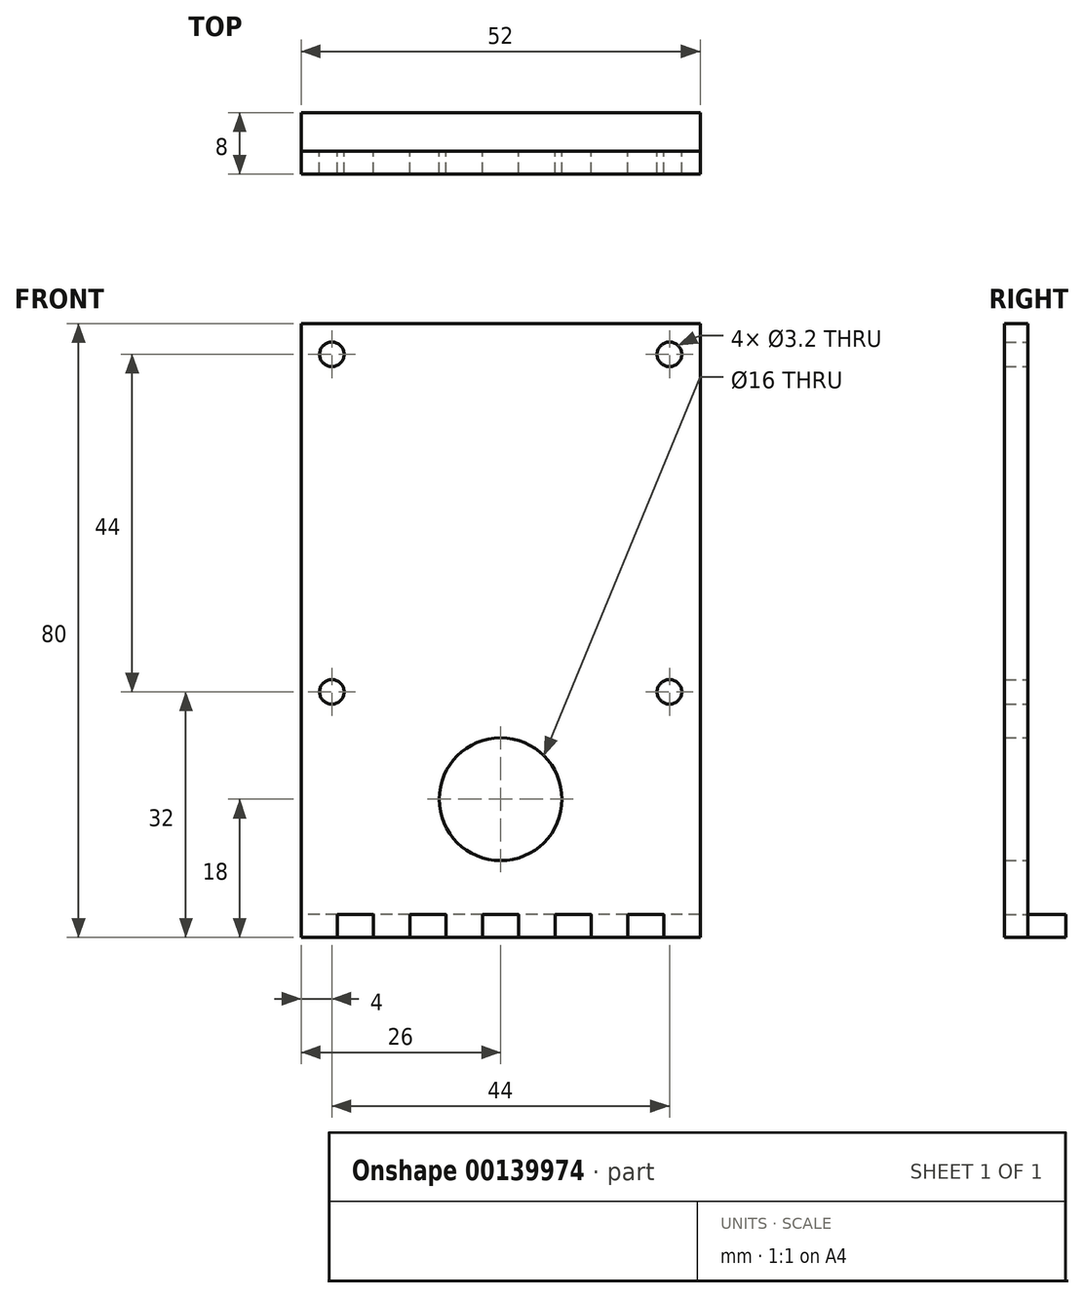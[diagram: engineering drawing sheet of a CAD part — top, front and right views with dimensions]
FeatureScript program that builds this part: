
annotation { "Feature Type Name" : "Feature", "Feature Type Description" : "" }
export const myFeature = defineFeature(function(context is Context, id is Id, definition is map)
    precondition{}
    {
        {
            var Q0;
            Q0=qCreatedBy(makeId("Front.planeOp"),FACE);
            var sketch = newSketch(context, id + "F0", { "sketchPlane" : qUnion([Q0])});
            skLineSegment(sketch, "E0.bottom", {"start": v(0, 0) * mm, "end": v(4.73, 0) * mm});
            skLineSegment(sketch, "E0.top", {"start": v(0, 80) * mm, "end": v(52, 80) * mm});
            skLineSegment(sketch, "E0.left", {"start": v(0, 0) * mm, "end": v(0, 80) * mm});
            skLineSegment(sketch, "E0.right", {"start": v(52, 0) * mm, "end": v(52, 80) * mm});
            skLineSegment(sketch, "E1", {"start": v(28.36, 3) * mm, "end": v(28.36, 0) * mm});
            skLineSegment(sketch, "E2", {"start": v(33.1, 0) * mm, "end": v(33.1, 3) * mm});
            skLineSegment(sketch, "E3", {"start": v(33.1, 3) * mm, "end": v(37.82, 3) * mm});
            skLineSegment(sketch, "E4", {"start": v(37.82, 3) * mm, "end": v(37.82, 0) * mm});
            skLineSegment(sketch, "E5", {"start": v(42.55, 0) * mm, "end": v(42.55, 3) * mm});
            skLineSegment(sketch, "E6", {"start": v(42.55, 3) * mm, "end": v(47.27, 3) * mm});
            skLineSegment(sketch, "E7", {"start": v(47.27, 3) * mm, "end": v(47.27, 0) * mm});
            skLineSegment(sketch, "E8.trimOffspring", {"start": v(28.36, 0) * mm, "end": v(33.1, 0) * mm});
            skLineSegment(sketch, "E9.trimOffspring", {"start": v(37.82, 0) * mm, "end": v(42.55, 0) * mm});
            skLineSegment(sketch, "E10.trimOffspring", {"start": v(47.27, 0) * mm, "end": v(52, 0) * mm});
            skLineSegment(sketch, "E11", {"start": v(4.73, 0) * mm, "end": v(4.73, 3) * mm});
            skLineSegment(sketch, "E12", {"start": v(4.73, 3) * mm, "end": v(9.45, 3) * mm});
            skLineSegment(sketch, "E13", {"start": v(9.45, 3) * mm, "end": v(9.45, 0) * mm});
            skLineSegment(sketch, "E14", {"start": v(9.45, 0) * mm, "end": v(14.18, 0) * mm});
            skLineSegment(sketch, "E15", {"start": v(14.18, 0) * mm, "end": v(14.18, 3) * mm});
            skLineSegment(sketch, "E16", {"start": v(14.18, 3) * mm, "end": v(18.9, 3) * mm});
            skLineSegment(sketch, "E17", {"start": v(18.9, 3) * mm, "end": v(18.9, 0) * mm});
            skLineSegment(sketch, "E18", {"start": v(18.9, 0) * mm, "end": v(23.64, 0) * mm});
            skLineSegment(sketch, "E19", {"start": v(23.64, 0) * mm, "end": v(23.64, 3) * mm});
            skLineSegment(sketch, "E20", {"start": v(23.64, 3) * mm, "end": v(28.36, 3) * mm});
            skLineSegment(sketch, "E21.bottom", {"start": v(4, 76) * mm, "end": v(48, 76) * mm, "construction": true});
            skLineSegment(sketch, "E21.top", {"start": v(4, 32) * mm, "end": v(48, 32) * mm, "construction": true});
            skLineSegment(sketch, "E21.left", {"start": v(4, 76) * mm, "end": v(4, 32) * mm, "construction": true});
            skLineSegment(sketch, "E21.right", {"start": v(48, 76) * mm, "end": v(48, 32) * mm, "construction": true});
            skLineSegment(sketch, "E22", {"start": v(0, 76) * mm, "end": v(4, 76) * mm, "construction": true});
            skLineSegment(sketch, "E23", {"start": v(4, 76) * mm, "end": v(4, 80) * mm, "construction": true});
            skLineSegment(sketch, "E24", {"start": v(48, 76) * mm, "end": v(52, 76) * mm, "construction": true});
            skCircle(sketch, "E25", {"center": v(4, 76) * mm, "radius": 1.6 * mm});
            skCircle(sketch, "E26", {"center": v(48, 76) * mm, "radius": 1.6 * mm});
            skCircle(sketch, "E27", {"center": v(4, 32) * mm, "radius": 1.6 * mm});
            skCircle(sketch, "E28", {"center": v(48, 32) * mm, "radius": 1.6 * mm});
            skCircle(sketch, "E29", {"center": v(26, 18) * mm, "radius": 8 * mm});
            skLineSegment(sketch, "E30", {"start": v(26, 80) * mm, "end": v(26, 32) * mm, "construction": true});
            skSolve(sketch);
        }
        {
            var Q0;
            Q0=makeQuery(id+"F0.imprint","IMPRINT",FACE,{"disambiguationData":[TD([[makeQuery(id+"F0.imprint","IMPRINT",EDGE,{"derivedFrom":sQuery(id+"F0.wireOp",EDGE,"E0.bottom")}),1.0]])]});
            var Q1;
            {var subQ6=sQuery(id+"F0.wireOp",EDGE,"E4");Q1=makeQuery(id+"F0.imprint","IMPRINT",FACE,{"disambiguationData":[TD([[makeQuery(id+"F0.imprint","IMPRINT",EDGE,{"derivedFrom":subQ6}),1.0]])]});}
            extrude(context, id + "F1", {"entities" : qUnion([Q0, Q1]), "depth" : 3 * mm});
        }
        {
            var Q0;
            Q0=makeQuery(id+"F1.opExtrude","CAP_FACE",FACE,{"disambiguationData":[OSD([sQuery(id+"F0.wireOp",EDGE,"E0.bottom"),sQuery(id+"F0.wireOp",EDGE,"E0.top"),sQuery(id+"F0.wireOp",EDGE,"E0.left"),sQuery(id+"F0.wireOp",EDGE,"E0.right"),sQuery(id+"F0.wireOp",EDGE,"E1"),sQuery(id+"F0.wireOp",EDGE,"E2"),sQuery(id+"F0.wireOp",EDGE,"E3"),sQuery(id+"F0.wireOp",EDGE,"E4"),sQuery(id+"F0.wireOp",EDGE,"E5"),sQuery(id+"F0.wireOp",EDGE,"E6"),sQuery(id+"F0.wireOp",EDGE,"PKkihstR-OvO3-Emr3-Gdbt-astjGcmU0KQB"),sQuery(id+"F0.wireOp",EDGE,"1ep62Iue-U5LH-vBv7-MXpD-Muabvh4OJFxf"),sQuery(id+"F0.wireOp",EDGE,"l2Q62QRf-urln-dHTa-iypO-8Orn8cwlWFba"),sQuery(id+"F0.wireOp",EDGE,"E7"),sQuery(id+"F0.wireOp",EDGE,"b9FiUV6K-tjbD-lqSt-eLXH-odPebWflUP3h"),sQuery(id+"F0.wireOp",EDGE,"AiMVLUEX-WyG6-zVHs-gMEj-qvYr0DqTvYnE"),sQuery(id+"F0.wireOp",EDGE,"VuksS3ty-KPdi-KyUG-c4xT-hWloxtrvA3Kk"),sQuery(id+"F0.wireOp",EDGE,"E8.trimOffspring"),sQuery(id+"F0.wireOp",EDGE,"E9.trimOffspring"),sQuery(id+"F0.wireOp",EDGE,"dc53b560-5744-44dd-9cf0-b4f1f6c820a9.trimOffspring"),sQuery(id+"F0.wireOp",EDGE,"b14e94e7-d7bf-4d2a-936f-5f05cbea75e0.trimOffspring"),sQuery(id+"F0.wireOp",EDGE,"E10.trimOffspring"),sQuery(id+"F0.wireOp",EDGE,"E11"),sQuery(id+"F0.wireOp",EDGE,"E12"),sQuery(id+"F0.wireOp",EDGE,"E13"),sQuery(id+"F0.wireOp",EDGE,"E14"),sQuery(id+"F0.wireOp",EDGE,"E15"),sQuery(id+"F0.wireOp",EDGE,"E16"),sQuery(id+"F0.wireOp",EDGE,"E17"),sQuery(id+"F0.wireOp",EDGE,"E18"),sQuery(id+"F0.wireOp",EDGE,"E19"),sQuery(id+"F0.wireOp",EDGE,"E20")])],"isStart":false});
            var sketch = newSketch(context, id + "F2", { "sketchPlane" : qUnion([Q0])});
            skLineSegment(sketch, "E31.bottom", {"start": v(0, 0) * mm, "end": v(52, 0) * mm});
            skLineSegment(sketch, "E31.top", {"start": v(0, 3) * mm, "end": v(52, 3) * mm});
            skLineSegment(sketch, "E31.left", {"start": v(0, 0) * mm, "end": v(0, 3) * mm});
            skLineSegment(sketch, "E31.right", {"start": v(52, 0) * mm, "end": v(52, 3) * mm});
            skSolve(sketch);
        }
        {
            var Q0;
            {var subQ0=sQuery(id+"F2.wireOp",EDGE,"E31.left");Q0=makeQuery(id+"F2.imprint","IMPRINT",FACE,{"disambiguationData":[TD([[makeQuery(id+"F2.imprint","IMPRINT",EDGE,{"derivedFrom":subQ0}),-1.0]])]});}
            var Q1;
            {var subQ1=makeQuery(id+"F1.opExtrude","CAP_EDGE",EDGE,{"disambiguationData":[OSD([sQuery(id+"F0.wireOp",EDGE,"E11")])],"isStart":false});Q1=makeQuery(id+"F2.imprint","IMPRINT",FACE,{"disambiguationData":[TD([[makeQuery(id+"F2.imprint","IMPRINT",EDGE,{"derivedFrom":subQ1}),-1.0]])]});}
            var Q2;
            {var subQ1=makeQuery(id+"F1.opExtrude","CAP_EDGE",EDGE,{"disambiguationData":[OSD([sQuery(id+"F0.wireOp",EDGE,"E13")])],"isStart":false});Q2=makeQuery(id+"F2.imprint","IMPRINT",FACE,{"disambiguationData":[TD([[makeQuery(id+"F2.imprint","IMPRINT",EDGE,{"derivedFrom":subQ1}),1.0]])]});}
            var Q3;
            {var subQ1=makeQuery(id+"F1.opExtrude","CAP_EDGE",EDGE,{"disambiguationData":[OSD([sQuery(id+"F0.wireOp",EDGE,"E15")])],"isStart":false});Q3=makeQuery(id+"F2.imprint","IMPRINT",FACE,{"disambiguationData":[TD([[makeQuery(id+"F2.imprint","IMPRINT",EDGE,{"derivedFrom":subQ1}),-1.0]])]});}
            var Q4;
            {var subQ1=makeQuery(id+"F1.opExtrude","CAP_EDGE",EDGE,{"disambiguationData":[OSD([sQuery(id+"F0.wireOp",EDGE,"E17")])],"isStart":false});Q4=makeQuery(id+"F2.imprint","IMPRINT",FACE,{"disambiguationData":[TD([[makeQuery(id+"F2.imprint","IMPRINT",EDGE,{"derivedFrom":subQ1}),1.0]])]});}
            var Q5;
            {var subQ1=makeQuery(id+"F1.opExtrude","CAP_EDGE",EDGE,{"disambiguationData":[OSD([sQuery(id+"F0.wireOp",EDGE,"E1")])],"isStart":false});Q5=makeQuery(id+"F2.imprint","IMPRINT",FACE,{"disambiguationData":[TD([[makeQuery(id+"F2.imprint","IMPRINT",EDGE,{"derivedFrom":subQ1}),-1.0]])]});}
            var Q6;
            {var subQ1=makeQuery(id+"F1.opExtrude","CAP_EDGE",EDGE,{"disambiguationData":[OSD([sQuery(id+"F0.wireOp",EDGE,"E1")])],"isStart":false});Q6=makeQuery(id+"F2.imprint","IMPRINT",FACE,{"disambiguationData":[TD([[makeQuery(id+"F2.imprint","IMPRINT",EDGE,{"derivedFrom":subQ1}),1.0]])]});}
            var Q7;
            {var subQ1=makeQuery(id+"F1.opExtrude","CAP_EDGE",EDGE,{"disambiguationData":[OSD([sQuery(id+"F0.wireOp",EDGE,"E2")])],"isStart":false});Q7=makeQuery(id+"F2.imprint","IMPRINT",FACE,{"disambiguationData":[TD([[makeQuery(id+"F2.imprint","IMPRINT",EDGE,{"derivedFrom":subQ1}),-1.0]])]});}
            var Q8;
            {var subQ1=makeQuery(id+"F1.opExtrude","CAP_EDGE",EDGE,{"disambiguationData":[OSD([sQuery(id+"F0.wireOp",EDGE,"E4")])],"isStart":false});Q8=makeQuery(id+"F2.imprint","IMPRINT",FACE,{"disambiguationData":[TD([[makeQuery(id+"F2.imprint","IMPRINT",EDGE,{"derivedFrom":subQ1}),1.0]])]});}
            var Q9;
            {var subQ1=makeQuery(id+"F1.opExtrude","CAP_EDGE",EDGE,{"disambiguationData":[OSD([sQuery(id+"F0.wireOp",EDGE,"E5")])],"isStart":false});Q9=makeQuery(id+"F2.imprint","IMPRINT",FACE,{"disambiguationData":[TD([[makeQuery(id+"F2.imprint","IMPRINT",EDGE,{"derivedFrom":subQ1}),-1.0]])]});}
            var Q10;
            {var subQ1=makeQuery(id+"F1.opExtrude","CAP_EDGE",EDGE,{"disambiguationData":[OSD([sQuery(id+"F0.wireOp",EDGE,"PKkihstR-OvO3-Emr3-Gdbt-astjGcmU0KQB")])],"isStart":false});Q10=makeQuery(id+"F2.imprint","IMPRINT",FACE,{"disambiguationData":[TD([[makeQuery(id+"F2.imprint","IMPRINT",EDGE,{"derivedFrom":subQ1}),1.0]])]});}
            var Q11;
            {var subQ1=makeQuery(id+"F1.opExtrude","CAP_EDGE",EDGE,{"disambiguationData":[OSD([sQuery(id+"F0.wireOp",EDGE,"1ep62Iue-U5LH-vBv7-MXpD-Muabvh4OJFxf")])],"isStart":false});Q11=makeQuery(id+"F2.imprint","IMPRINT",FACE,{"disambiguationData":[TD([[makeQuery(id+"F2.imprint","IMPRINT",EDGE,{"derivedFrom":subQ1}),-1.0]])]});}
            var Q12;
            {var subQ1=makeQuery(id+"F1.opExtrude","CAP_EDGE",EDGE,{"disambiguationData":[OSD([sQuery(id+"F0.wireOp",EDGE,"E7")])],"isStart":false});Q12=makeQuery(id+"F2.imprint","IMPRINT",FACE,{"disambiguationData":[TD([[makeQuery(id+"F2.imprint","IMPRINT",EDGE,{"derivedFrom":subQ1}),1.0]])]});}
            var Q13;
            {var subQ1=makeQuery(id+"F1.opExtrude","CAP_EDGE",EDGE,{"disambiguationData":[OSD([sQuery(id+"F0.wireOp",EDGE,"b9FiUV6K-tjbD-lqSt-eLXH-odPebWflUP3h")])],"isStart":false});Q13=makeQuery(id+"F2.imprint","IMPRINT",FACE,{"disambiguationData":[TD([[makeQuery(id+"F2.imprint","IMPRINT",EDGE,{"derivedFrom":subQ1}),-1.0]])]});}
            var Q14;
            {var subQ0=sQuery(id+"F2.wireOp",EDGE,"E31.right");Q14=makeQuery(id+"F2.imprint","IMPRINT",FACE,{"disambiguationData":[TD([[makeQuery(id+"F2.imprint","IMPRINT",EDGE,{"derivedFrom":subQ0}),1.0]])]});}
            extrude(context, id + "F3", {"entities" : qUnion([Q0, Q1, Q2, Q3, Q4, Q5, Q6, Q7, Q8, Q9, Q10, Q11, Q12, Q13, Q14]), "oppositeDirection" : true, "depth" : 8 * mm});
        }
        {
            var Q0;
            Q0=makeQuery(id+"F1.opExtrude","SWEPT_BODY",BODY,{"disambiguationData":[OSD([sQuery(id+"F0.wireOp",EDGE,"E0.bottom"),sQuery(id+"F0.wireOp",EDGE,"E0.top"),sQuery(id+"F0.wireOp",EDGE,"E0.left"),sQuery(id+"F0.wireOp",EDGE,"E0.right"),sQuery(id+"F0.wireOp",EDGE,"E1"),sQuery(id+"F0.wireOp",EDGE,"E2"),sQuery(id+"F0.wireOp",EDGE,"E3"),sQuery(id+"F0.wireOp",EDGE,"E4"),sQuery(id+"F0.wireOp",EDGE,"E5"),sQuery(id+"F0.wireOp",EDGE,"E6"),sQuery(id+"F0.wireOp",EDGE,"PKkihstR-OvO3-Emr3-Gdbt-astjGcmU0KQB"),sQuery(id+"F0.wireOp",EDGE,"1ep62Iue-U5LH-vBv7-MXpD-Muabvh4OJFxf"),sQuery(id+"F0.wireOp",EDGE,"l2Q62QRf-urln-dHTa-iypO-8Orn8cwlWFba"),sQuery(id+"F0.wireOp",EDGE,"E7"),sQuery(id+"F0.wireOp",EDGE,"b9FiUV6K-tjbD-lqSt-eLXH-odPebWflUP3h"),sQuery(id+"F0.wireOp",EDGE,"AiMVLUEX-WyG6-zVHs-gMEj-qvYr0DqTvYnE"),sQuery(id+"F0.wireOp",EDGE,"VuksS3ty-KPdi-KyUG-c4xT-hWloxtrvA3Kk"),sQuery(id+"F0.wireOp",EDGE,"E8.trimOffspring"),sQuery(id+"F0.wireOp",EDGE,"E9.trimOffspring"),sQuery(id+"F0.wireOp",EDGE,"dc53b560-5744-44dd-9cf0-b4f1f6c820a9.trimOffspring"),sQuery(id+"F0.wireOp",EDGE,"b14e94e7-d7bf-4d2a-936f-5f05cbea75e0.trimOffspring"),sQuery(id+"F0.wireOp",EDGE,"E10.trimOffspring"),sQuery(id+"F0.wireOp",EDGE,"E11"),sQuery(id+"F0.wireOp",EDGE,"E12"),sQuery(id+"F0.wireOp",EDGE,"E13"),sQuery(id+"F0.wireOp",EDGE,"E14"),sQuery(id+"F0.wireOp",EDGE,"E15"),sQuery(id+"F0.wireOp",EDGE,"E16"),sQuery(id+"F0.wireOp",EDGE,"E17"),sQuery(id+"F0.wireOp",EDGE,"E18"),sQuery(id+"F0.wireOp",EDGE,"E19"),sQuery(id+"F0.wireOp",EDGE,"E20")])]});
            var Q1;
            Q1=makeQuery(id+"F3.opExtrude","SWEPT_BODY",BODY,{"disambiguationData":[OSD([sQuery(id+"F2.wireOp",EDGE,"E31.bottom"),sQuery(id+"F2.wireOp",EDGE,"E31.top"),sQuery(id+"F2.wireOp",EDGE,"E31.left"),sQuery(id+"F2.wireOp",EDGE,"E31.right")])]});
            booleanBodies(context, id + "F4", {"operationType" : BooleanOperationType.SUBTRACTION, "tools" : qUnion([Q0]), "targets" : qUnion([Q1]), "keepTools" : true});
        }
    });
